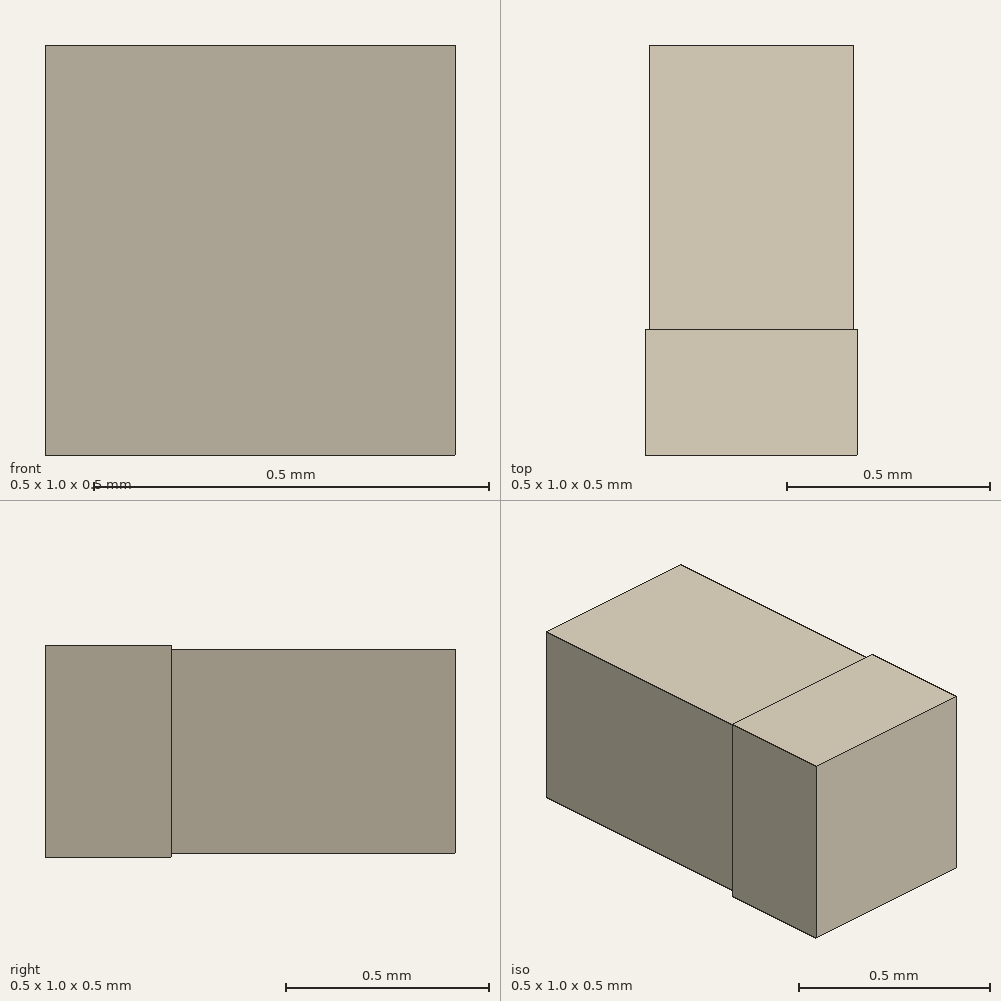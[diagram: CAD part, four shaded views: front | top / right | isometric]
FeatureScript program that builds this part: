
annotation { "Feature Type Name" : "Feature", "Feature Type Description" : "" }
export const myFeature = defineFeature(function(context is Context, id is Id, definition is map)
    precondition{}
    {
        {
            assignVariable(context, id + "F0", {"variableType" : VariableType.LENGTH, "name" : "LENGTH", "lengthValue" : 1 * mm});
        }
        {
            var Q0;
            Q0=qCreatedBy(makeId("Front.planeOp"),FACE);
            var sketch = newSketch(context, id + "F1", { "sketchPlane" : qUnion([Q0])});
            skLineSegment(sketch, "E0.bottom", {"start": v(0.25, 0.01) * mm, "end": v(-0.25, 0) * mm});
            skLineSegment(sketch, "E0.top", {"start": v(0.25, 0.51) * mm, "end": v(-0.25, 0.51) * mm});
            skLineSegment(sketch, "E0.left", {"start": v(0.25, 0.01) * mm, "end": v(0.25, 0.51) * mm});
            skLineSegment(sketch, "E0.right", {"start": v(-0.25, 0.01) * mm, "end": v(-0.25, 0.51) * mm});
            skPoint(sketch, "E0.middle", {"position": v(0, 0.26) * mm});
            skSolve(sketch);
        }
        {
            var Q0;
            Q0=qSketchRegion(id+"F1",true);
            extrude(context, id + "F2", {"entities" : qUnion([Q0]), "flatOperationType" : FlatOperationType.REMOVE, "offsetDistance" : 25 * mm, "depth" : getVariable(context, 'LENGTH'), "domain" : OperationDomain.MODEL, "symmetric" : true});
        }
        {
            var Q0;
            Q0=makeQuery(id+"F2.opExtrude","CAP_FACE",FACE,{"disambiguationData":[OSD([sQuery(id+"F1.wireOp",EDGE,"E0.bottom"),sQuery(id+"F1.wireOp",EDGE,"E0.top"),sQuery(id+"F1.wireOp",EDGE,"E0.left"),sQuery(id+"F1.wireOp",EDGE,"E0.right")])],"isStart":false});
            var sketch = newSketch(context, id + "F3", { "sketchPlane" : qUnion([Q0])});
            skLineSegment(sketch, "E1.0", {"start": v(-0.26, 0) * mm, "end": v(0.26, 0) * mm});
            skLineSegment(sketch, "E1.1", {"start": v(-0.26, 0.52) * mm, "end": v(-0.26, 0) * mm});
            skLineSegment(sketch, "E1.2", {"start": v(0.26, 0.52) * mm, "end": v(-0.26, 0.52) * mm});
            skLineSegment(sketch, "E1.3", {"start": v(0.26, 0) * mm, "end": v(0.26, 0.52) * mm});
            skSolve(sketch);
        }
        {
            var Q0;
            Q0=qSketchRegion(id+"F3",true);
            extrude(context, id + "F4", {"entities" : qUnion([Q0]), "flatOperationType" : FlatOperationType.REMOVE, "oppositeDirection" : true, "offsetDistance" : 25 * mm, "depth" : 0.3 * mm, "hasSecondDirection" : true, "secondDirectionOppositeDirection" : false, "secondDirectionDepth" : 0.01 * mm, "domain" : OperationDomain.MODEL});
        }
    });
